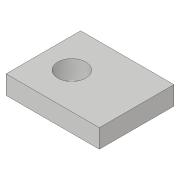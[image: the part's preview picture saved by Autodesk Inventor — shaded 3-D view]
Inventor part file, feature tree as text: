
AUTODESK INVENTOR PART (.ipt)
format: ipt  version: 2019 (Build 230136000, 136)  size: 80,384 bytes
history: native  units: in
note: dims shown in document units (in); Inventor stores cm internally (conversion verified against a paired STEP export)
features: extrude x2, sketch x2
ambient origin geometry x8: Origin, YZ Plane, XZ Plane, XY Plane, X Axis, Y Axis, Z Axis, Center Point
bodies: Solid1 (feature_tree)
feature tree (4):
  extrude  "Extrusion1"  Depth=1.5748in
  extrude  "Extrusion2"  Depth=0.3937in
  sketch  "Sketch1"  dims[d0=1.9685in d1=1.5748in]
  sketch  "Sketch2"  dims[d2=0.3937in d3=0.0in d4=0.5906in d5=0.3937in d6=0.0in]
